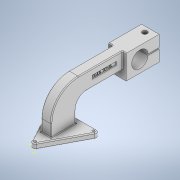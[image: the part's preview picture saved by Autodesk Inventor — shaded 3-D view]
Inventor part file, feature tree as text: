
AUTODESK INVENTOR PART (.ipt)
format: ipt  version: 2021 (Build 250183000, 183)  size: 290,304 bytes
history: native  units: in
note: dims shown in document units (in); Inventor stores cm internally (conversion verified against a paired STEP export)
features: sketch x10, extrude x7, fillet x3
ambient origin geometry x8: Origin, YZ Plane, XZ Plane, XY Plane, X Axis, Y Axis, Z Axis, Center Point
bodies: Solid1 (feature_tree)
feature tree (20):
  extrude  "Extrusion1"  Depth=17.7165in
  fillet  "Fillet1"  Radius=17.7165in
  extrude  "Extrusion2"  Depth=1.5748in
  fillet  "Fillet2"  Radius=3.937in
  extrude  "Extrusion3"  Depth=1.5748in
  extrude  "Extrusion4"  Depth=1.9685in
  fillet  "Fillet3"  Radius=3.937in
  extrude  "Extrusion5"  Depth=0.656in
  extrude  "Extrusion6"  Depth=7.0866in
  extrude  "Extrusion7"  Depth=8.6614in TaperAngle=0.0deg
  sketch  "Sketch8"  dims[d19=0.4685in]
  sketch  "Sketch9"  dims[d20=19.685in]
  sketch  "Sketch10"  dims[d21=19.685in d22=7.874in d23=23.622in d24=19.685in d25=7.874in d26=7.874in d27=7.0866in d28=0.0in d29=2.7559in d30=12.5984in d31=17.3228in d32=23.622in d33=0.0in d34=0.5935in d35=13.7795in d36=8.6614in d37=11.811in d38=0.3937in d39=0.7874in d40=23.6905in d41=0.0in d42=6.2992in d43=3.937in d44=3.5433in d45=26.747in d46=0.0in d47=0.628in d48=0.0in]
  sketch  "Sketch1"  dims[d0=33.4646in d1=17.7165in d2=17.7165in]
  sketch  "Sketch2"  dims[d3=3.937in d4=1.5748in d5=3.937in]
  sketch  "Sketch3"  dims[d6=3.937in d7=1.5748in]
  sketch  "Sketch4"  dims[d8=1.5748in d9=1.9685in d10=3.937in d11=0.0in]
  sketch  "Sketch5"  dims[d12=0.656in d13=7.874in]
  sketch  "Sketch6"  dims[d14=3.5433in d15=7.0866in]
  sketch  "Sketch7"  dims[d16=17.7165in d17=8.6614in d18=0.0in]
